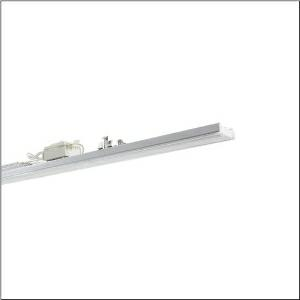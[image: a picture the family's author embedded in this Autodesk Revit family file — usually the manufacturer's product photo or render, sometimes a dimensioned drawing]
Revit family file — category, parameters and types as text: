
# Revit family: licross_r__21_recessed_mo_51te18vn445g_d29f
name_source: partatom
category: Lighting Fixtures
units: mm (PartAtom-declared; Revit-internal decimal feet)

## family parameters
Cut with Voids When Loaded = No
Host = Face
Light Source = No
Part Type = Normal
Room Calculation Point = No
Round Connector Dimension = Use Diameter
Shared = No

## types (1)
- --- (1 x LED, 4500 lm, 24.6 W, 4000K)
    Apparent Load = 25 VA
    CIE Flux Codes = 83 96 99 100 100
    Color Rendering = 80
    Color Temperature = 4000K
    Default Elevation = 1800 mm
    Description = Licross® 21 Recessed MO, luminaire insert, of sheet steel, galvanised, coil coated, white, length: 1.500mm, width: 66mm, height: 67mm, LED rated luminous flux: 4.500lm, light colour: 840, control gear: DALI 2, CLO, with plug, 5-pole, with phase selection, mains connection: 220..240V, AC, 50/60Hz, start of lifetime: 25W, end of service life: 27W, internal wiring halogen-free, primary light control with lens, of plastic, primary optical cover: cover, of PMMA, light emission: direct distribution, primary light characteristic: symmetric, protection rating (complete): IP54, insulation class (complete): insulation class I (protective earthing), certification: CE, ENEC, VDE, UKCA, protection symbol: D if used in an environment with non-conductive dust loads with corresponding accessories, impact resistance: IK06, permissible ambient temperature for indoor applications: -25..+45°C, corresponds to IFS (International Featured Standards) requirements for safety and quality in the food industry, reducing of maximum allowable ambient temperature of 5°C with ceiling mounting, LABS conformity tested according to VDMA 24364:2018-05, packaging unit: 1 piece
    Height = 58 mm
    Lamp = 1 x LED
    Lamp Light Flux = 4500 lm
    Lamp Power = 24.6 W
    Lamp count = 1
    Length = 1500 mm
    Luminous efficacy = 183 lm/W
    Manufacturer = Siteco
    ModVariant = No
    Model = 51TE18VN445G
    Mounting Place = Ceiling
    Mounting Type = Pendant
    Number of Poles = 1
    OnlyDefault = Yes
    Power Factor = 1
    Product Name = Licross® 21 Recessed MO
    Product group = luminaire insert | ceiling pendant
    ProductGroupID = 902
    Protection Class = Protection class I
    Protection Degree = IP 54
    RLX_Detail_Level = 1
    RLX_Emergency_Light_Flux = 0 lm
    RLX_Emergency_Type = 0
    RLX_Emergency_Type_DB = No
    RlxData = <blob elided: 24245 chars, md5=5b886fe6>
    Socket = socket
    Standby Power = 0 W
    System Light Flux = 4500 lm
    System Power = 25 W
    Type Comments = factory setting: luminous flux: 100 % | dim-lin: 254 | 163 mA
    Type Image = l_1296930.jpg
    URL = http://relux.com
    VarID = @adj_108611
    Voltage = 0 V
    Weight = 0.00 kg
    Width = 66 mm

## geometry (parser evidence)
native form markers: Blend x4, Sweep x12
no freeform markers — native parametric forms only
